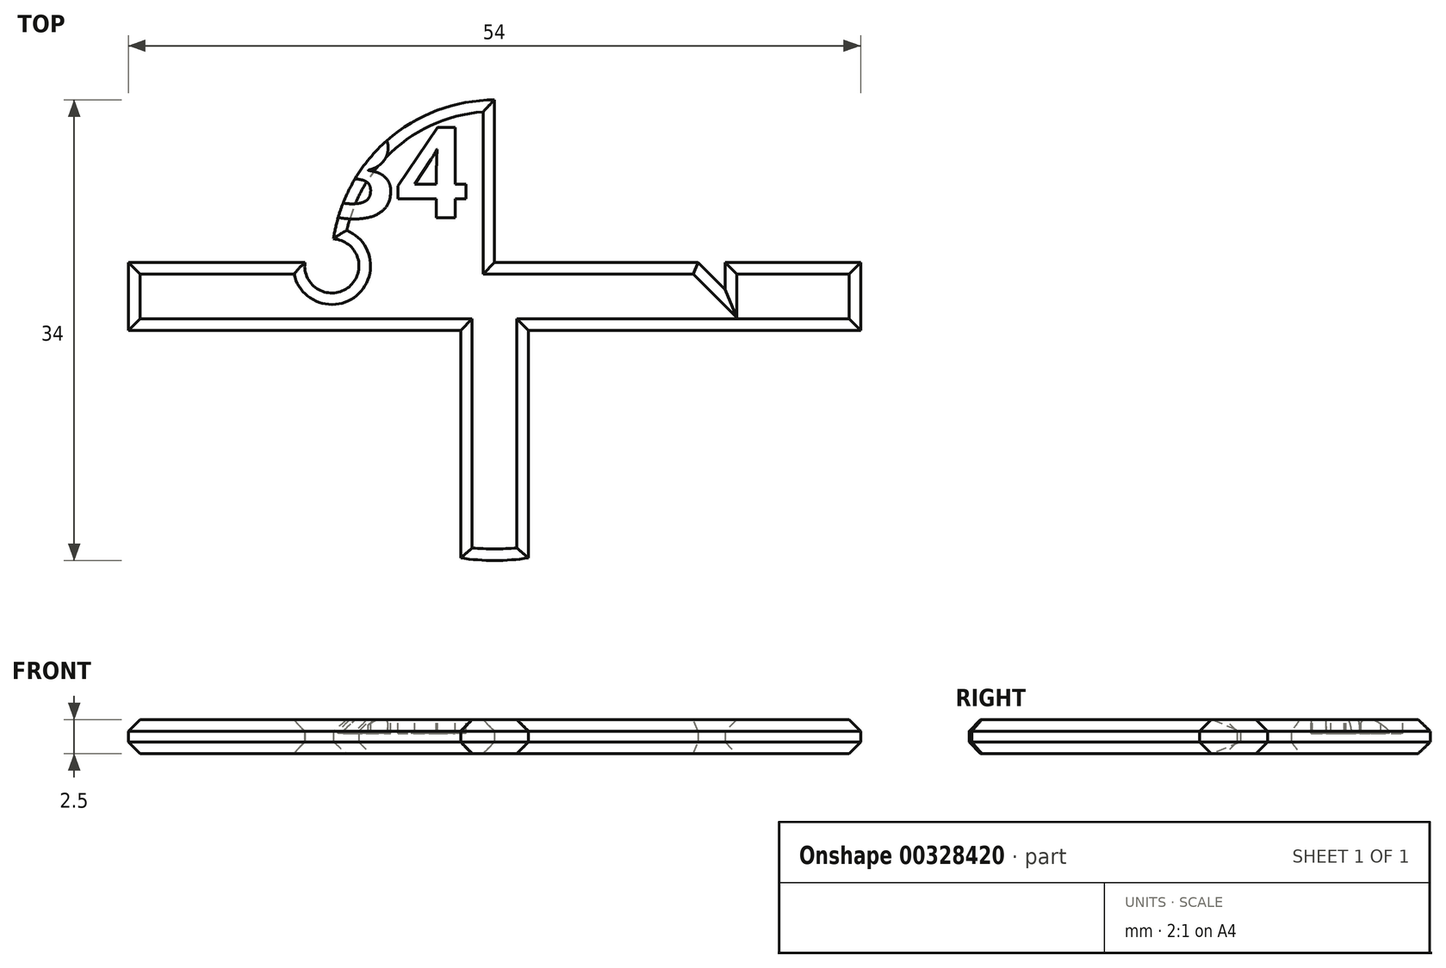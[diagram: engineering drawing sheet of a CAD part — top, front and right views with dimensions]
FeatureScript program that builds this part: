
annotation { "Feature Type Name" : "Feature", "Feature Type Description" : "" }
export const myFeature = defineFeature(function(context is Context, id is Id, definition is map)
    precondition{}
    {
        {
            var Q0;
            Q0=qCreatedBy(makeId("Top.planeOp"),FACE);
            var sketch = newSketch(context, id + "F0", { "sketchPlane" : qUnion([Q0])});
            skLineSegment(sketch, "E0", {"start": v(0, 0) * mm, "end": v(-17, 0) * mm});
            skArc(sketch, "E1", {"start": v(-17, 0) * mm, "mid": v(-12.02, 12.02) * mm, "end": v(0, 17) * mm});
            skLineSegment(sketch, "E2", {"start": v(0, 17) * mm, "end": v(0, 0) * mm});
            skArc(sketch, "E3", {"start": v(0, 17) * mm, "mid": v(12.02, 12.02) * mm, "end": v(17, 0) * mm, "construction": true});
            skLineSegment(sketch, "E4", {"start": v(0, 0) * mm, "end": v(17, 0) * mm});
            skLineSegment(sketch, "E5", {"start": v(17, 0) * mm, "end": v(27, 0) * mm});
            skLineSegment(sketch, "E6", {"start": v(27, 0) * mm, "end": v(27, -5) * mm});
            skLineSegment(sketch, "E7", {"start": v(27, -5) * mm, "end": v(-27, -5) * mm});
            skLineSegment(sketch, "E8", {"start": v(-27, -5) * mm, "end": v(-27, 0) * mm});
            skLineSegment(sketch, "E9", {"start": v(-27, 0) * mm, "end": v(-17, 0) * mm});
            skLineSegment(sketch, "E10", {"start": v(0, -5) * mm, "end": v(0, -22) * mm, "construction": true});
            skPoint(sketch, "E10.endSnap0", {"position": v(0, -5) * mm});
            skArc(sketch, "E11", {"start": v(0, -22) * mm, "mid": v(1.25, -21.95) * mm, "end": v(2.5, -21.82) * mm});
            skArc(sketch, "E12", {"start": v(0, -22) * mm, "mid": v(-1.25, -21.95) * mm, "end": v(-2.5, -21.82) * mm});
            skLineSegment(sketch, "E13", {"start": v(-2.5, -21.82) * mm, "end": v(-2.5, -5) * mm});
            skLineSegment(sketch, "E14", {"start": v(2.5, -21.82) * mm, "end": v(2.5, -5) * mm});
            skLineSegment(sketch, "E15", {"start": v(17, 0) * mm, "end": v(17, -2) * mm});
            skPoint(sketch, "E16", {"position": v(15, 0) * mm});
            skLineSegment(sketch, "E17", {"start": v(15, 0) * mm, "end": v(17, -2) * mm});
            skArc(sketch, "E18", {"start": v(-12, 0) * mm, "mid": v(-8.49, 8.49) * mm, "end": v(0, 12) * mm});
            skLineSegment(sketch, "E19", {"start": v(-7, 0) * mm, "end": v(-7, 9.75) * mm});
            skLineSegment(sketch, "E20", {"start": v(-7, -0.25) * mm, "end": v(-17, -0.25) * mm, "construction": true});
            skCircle(sketch, "E21", {"center": v(-12, -0.25) * mm, "radius": 2 * mm});
            skSolve(sketch);
        }
        {
            var Q0;
            Q0=makeQuery(id+"F0.imprint","IMPRINT",FACE,{"disambiguationData":[TD([[makeQuery(id+"F0.imprint","IMPRINT",EDGE,{"derivedFrom":sQuery(id+"F0.wireOp",EDGE,"E11")}),1.0]])]});
            var Q1;
            {var subQ0=sQuery(id+"F0.wireOp",EDGE,"E1");Q1=makeQuery(id+"F0.imprint","IMPRINT",FACE,{"disambiguationData":[TD([[makeQuery(id+"F0.imprint","IMPRINT",EDGE,{"derivedFrom":subQ0}),-1.0]])]});}
            var Q2;
            {var subQ3=sQuery(id+"F0.wireOp",EDGE,"E19");Q2=makeQuery(id+"F0.imprint","IMPRINT",FACE,{"disambiguationData":[TD([[makeQuery(id+"F0.imprint","IMPRINT",EDGE,{"derivedFrom":subQ3}),1.0]])]});}
            var Q3;
            Q3=makeQuery(id+"F0.imprint","IMPRINT",FACE,{"disambiguationData":[TD([[makeQuery(id+"F0.imprint","IMPRINT",EDGE,{"derivedFrom":sQuery(id+"F0.wireOp",EDGE,"E5")}),-1.0]])]});
            var Q4;
            {var subQ3=sQuery(id+"F0.wireOp",EDGE,"E19");Q4=makeQuery(id+"F0.imprint","IMPRINT",FACE,{"disambiguationData":[TD([[makeQuery(id+"F0.imprint","IMPRINT",EDGE,{"derivedFrom":subQ3}),-1.0]])]});}
            extrude(context, id + "F1", {"entities" : qUnion([Q0, Q1, Q2, Q3, Q4]), "depth" : 2.5 * mm});
        }
        {
            var Q0;
            Q0=makeQuery(id+"F1.opExtrude","CAP_FACE",FACE,{"disambiguationData":[OSD([sQuery(id+"F0.wireOp",EDGE,"E1"),sQuery(id+"F0.wireOp",EDGE,"E2"),sQuery(id+"F0.wireOp",EDGE,"E4"),sQuery(id+"F0.wireOp",EDGE,"E5"),sQuery(id+"F0.wireOp",EDGE,"E6"),sQuery(id+"F0.wireOp",EDGE,"E7"),sQuery(id+"F0.wireOp",EDGE,"E8"),sQuery(id+"F0.wireOp",EDGE,"E9"),sQuery(id+"F0.wireOp",EDGE,"E11"),sQuery(id+"F0.wireOp",EDGE,"E12"),sQuery(id+"F0.wireOp",EDGE,"E13"),sQuery(id+"F0.wireOp",EDGE,"E14")])],"isStart":false});
            var Q1;
            Q1=makeQuery(id+"F1.opExtrude","CAP_FACE",FACE,{"disambiguationData":[OSD([sQuery(id+"F0.wireOp",EDGE,"E1"),sQuery(id+"F0.wireOp",EDGE,"E2"),sQuery(id+"F0.wireOp",EDGE,"E4"),sQuery(id+"F0.wireOp",EDGE,"E5"),sQuery(id+"F0.wireOp",EDGE,"E6"),sQuery(id+"F0.wireOp",EDGE,"E7"),sQuery(id+"F0.wireOp",EDGE,"E8"),sQuery(id+"F0.wireOp",EDGE,"E9"),sQuery(id+"F0.wireOp",EDGE,"E11"),sQuery(id+"F0.wireOp",EDGE,"E12"),sQuery(id+"F0.wireOp",EDGE,"E13"),sQuery(id+"F0.wireOp",EDGE,"E14")])],"isStart":true});
            chamfer(context, id + "F2", {"entities" : qUnion([Q0, Q1]), "width" : .85 * mm, "tangentPropagation" : true});
        }
        {
            var Q0;
            Q0=makeQuery(id+"F1.opExtrude","CAP_FACE",FACE,{"disambiguationData":[OSD([sQuery(id+"F0.wireOp",EDGE,"E1"),sQuery(id+"F0.wireOp",EDGE,"E2"),sQuery(id+"F0.wireOp",EDGE,"E4"),sQuery(id+"F0.wireOp",EDGE,"E5"),sQuery(id+"F0.wireOp",EDGE,"E6"),sQuery(id+"F0.wireOp",EDGE,"E7"),sQuery(id+"F0.wireOp",EDGE,"E8"),sQuery(id+"F0.wireOp",EDGE,"E9"),sQuery(id+"F0.wireOp",EDGE,"E11"),sQuery(id+"F0.wireOp",EDGE,"E12"),sQuery(id+"F0.wireOp",EDGE,"E13"),sQuery(id+"F0.wireOp",EDGE,"E14")])],"isStart":false});
            var sketch = newSketch(context, id + "F3", { "sketchPlane" : qUnion([Q0])});
            skText(sketch, "E22", { "text": "34", "fontName": "OpenSans-Bold.ttf"});
            const initialGuessF3  = {"E22": [-0.01264, 0.0033, 1, 0, 0.00674]};
            skSetInitialGuess(sketch, initialGuessF3);
            skSolve(sketch);
        }
        {
            var Q0;
            Q0 = qSketchRegion(id + "F3", true);
            extrude(context, id + "F4", {"entities" : qUnion([Q0]), "operationType" : NewBodyOperationType.REMOVE, "oppositeDirection" : true, "depth" : 1 * mm});
        }
    });
